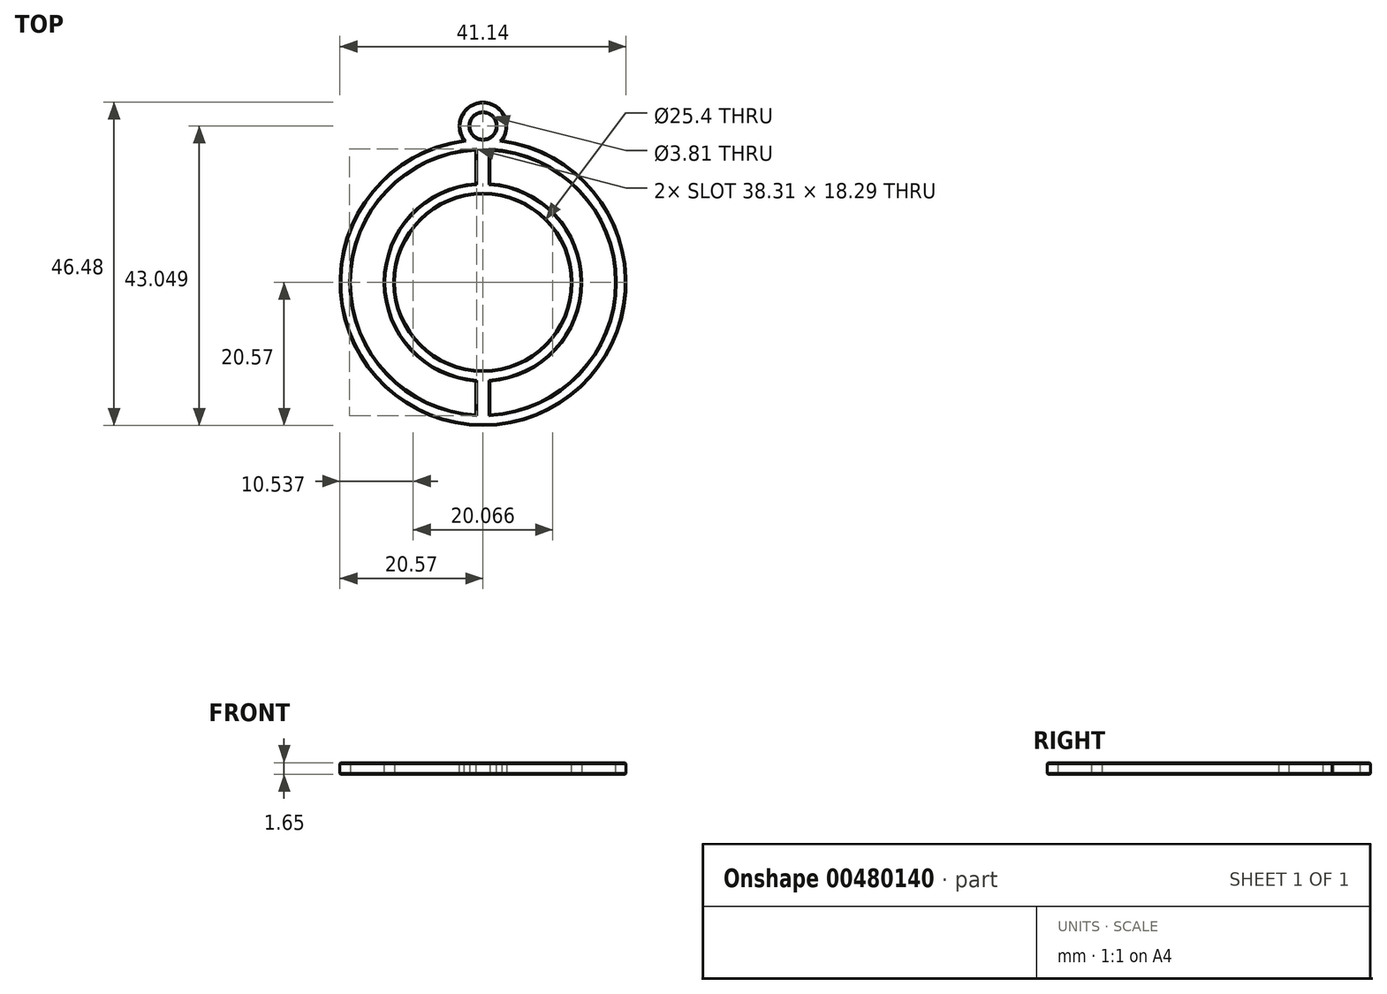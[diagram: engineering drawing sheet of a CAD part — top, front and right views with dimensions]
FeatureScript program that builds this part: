
annotation { "Feature Type Name" : "Feature", "Feature Type Description" : "" }
export const myFeature = defineFeature(function(context is Context, id is Id, definition is map)
    precondition{}
    {
        {
            var Q0;
            Q0=qCreatedBy(makeId("Top.planeOp"),FACE);
            var sketch = newSketch(context, id + "F0", { "sketchPlane" : qUnion([Q0])});
            skArc(sketch, "E0", {"start": v(-1.02, 19.02) * mm, "mid": v(-19.05, 0) * mm, "end": v(-1.02, -19.02) * mm});
            skArc(sketch, "E1.0", {"start": v(-2.72, 20.4) * mm, "mid": v(0, -20.57) * mm, "end": v(2.72, 20.4) * mm});
            skCircle(sketch, "E2", {"center": v(0, 0) * mm, "radius": 12.7 * mm});
            skArc(sketch, "E3.0", {"start": v(-1.02, 14.19) * mm, "mid": v(-14.22, 0) * mm, "end": v(-1.02, -14.19) * mm});
            skLineSegment(sketch, "E4.trimOffspring", {"start": v(-1.02, 19.02) * mm, "end": v(-1.02, 14.19) * mm});
            skLineSegment(sketch, "E5.trimOffspring", {"start": v(1.02, 19.02) * mm, "end": v(1.02, 14.19) * mm});
            skLineSegment(sketch, "E6.trimOffspring", {"start": v(-1.02, -14.19) * mm, "end": v(-1.02, -19.02) * mm});
            skLineSegment(sketch, "E7.trimOffspring", {"start": v(1.02, -14.19) * mm, "end": v(1.02, -19.02) * mm});
            skArc(sketch, "E8.trimOffspring", {"start": v(1.02, -14.19) * mm, "mid": v(14.22, 0) * mm, "end": v(1.02, 14.19) * mm});
            skArc(sketch, "E9.trimOffspring", {"start": v(1.02, -19.02) * mm, "mid": v(19.05, 0) * mm, "end": v(1.02, 19.02) * mm});
            skCircle(sketch, "E10", {"center": v(0, 22.48) * mm, "radius": 1.9 * mm});
            skArc(sketch, "E11.0", {"start": v(2.72, 20.4) * mm, "mid": v(0, 25.9) * mm, "end": v(-2.72, 20.4) * mm});
            skSolve(sketch);
        }
        {
            var Q0;
            Q0=makeQuery(id+"F0.imprint","IMPRINT",FACE,{"disambiguationData":[TD([[makeQuery(id+"F0.imprint","IMPRINT",EDGE,{"derivedFrom":sQuery(id+"F0.wireOp",EDGE,"E0")}),-1.0]])]});
            extrude(context, id + "F1", {"entities" : qUnion([Q0]), "depth" : 1.65 * mm});
        }
        {
            var Q0;
            Q0=makeQuery(id+"F1.opExtrude","CAP_FACE",FACE,{"disambiguationData":[OSD([sQuery(id+"F0.wireOp",EDGE,"E0"),sQuery(id+"F0.wireOp",EDGE,"E1.0"),sQuery(id+"F0.wireOp",EDGE,"E2"),sQuery(id+"F0.wireOp",EDGE,"E3.0"),sQuery(id+"F0.wireOp",EDGE,"E4.trimOffspring"),sQuery(id+"F0.wireOp",EDGE,"E5.trimOffspring"),sQuery(id+"F0.wireOp",EDGE,"E6.trimOffspring"),sQuery(id+"F0.wireOp",EDGE,"E7.trimOffspring"),sQuery(id+"F0.wireOp",EDGE,"E8.trimOffspring"),sQuery(id+"F0.wireOp",EDGE,"E9.trimOffspring"),sQuery(id+"F0.wireOp",EDGE,"E10"),sQuery(id+"F0.wireOp",EDGE,"E11.0")])],"isStart":false});
            var Q1;
            Q1=makeQuery(id+"F1.opExtrude","CAP_FACE",FACE,{"disambiguationData":[OSD([sQuery(id+"F0.wireOp",EDGE,"E0"),sQuery(id+"F0.wireOp",EDGE,"E1.0"),sQuery(id+"F0.wireOp",EDGE,"E2"),sQuery(id+"F0.wireOp",EDGE,"E3.0"),sQuery(id+"F0.wireOp",EDGE,"E4.trimOffspring"),sQuery(id+"F0.wireOp",EDGE,"E5.trimOffspring"),sQuery(id+"F0.wireOp",EDGE,"E6.trimOffspring"),sQuery(id+"F0.wireOp",EDGE,"E7.trimOffspring"),sQuery(id+"F0.wireOp",EDGE,"E8.trimOffspring"),sQuery(id+"F0.wireOp",EDGE,"E9.trimOffspring"),sQuery(id+"F0.wireOp",EDGE,"E10"),sQuery(id+"F0.wireOp",EDGE,"E11.0")])],"isStart":true});
            chamfer(context, id + "F2", {"entities" : qUnion([Q0, Q1]), "width" : 0.13 * mm, "tangentPropagation" : true});
        }
    });
